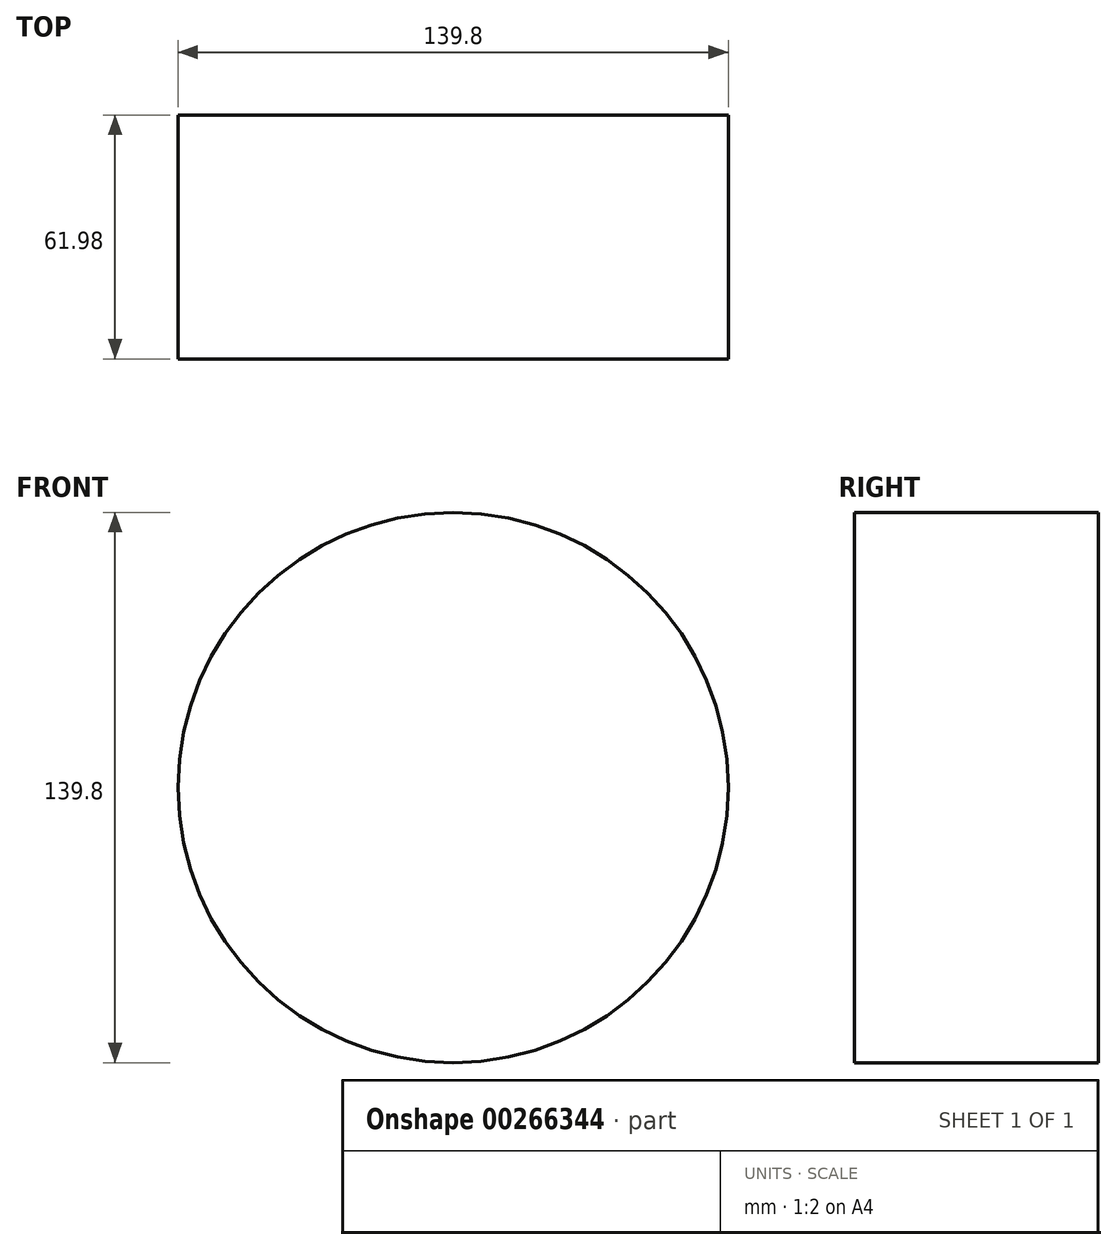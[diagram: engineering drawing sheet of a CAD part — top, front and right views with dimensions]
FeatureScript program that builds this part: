
annotation { "Feature Type Name" : "Feature", "Feature Type Description" : "" }
export const myFeature = defineFeature(function(context is Context, id is Id, definition is map)
    precondition{}
    {
        {
            var Q0;
            Q0=qCreatedBy(makeId("Front.planeOp"),FACE);
            var sketch = newSketch(context, id + "F0", { "sketchPlane" : qUnion([Q0])});
            skCircle(sketch, "E0", {"center": v(0, 0) * mm, "radius": 69.9 * mm});
            skSolve(sketch);
        }
        {
            var Q0;
            Q0 = qSketchRegion(id + "F0", true);
            extrude(context, id + "F1", {"entities" : qUnion([Q0]), "endBound" : BoundingType.SYMMETRIC, "depth" : 61.98 * mm});
        }
    });
